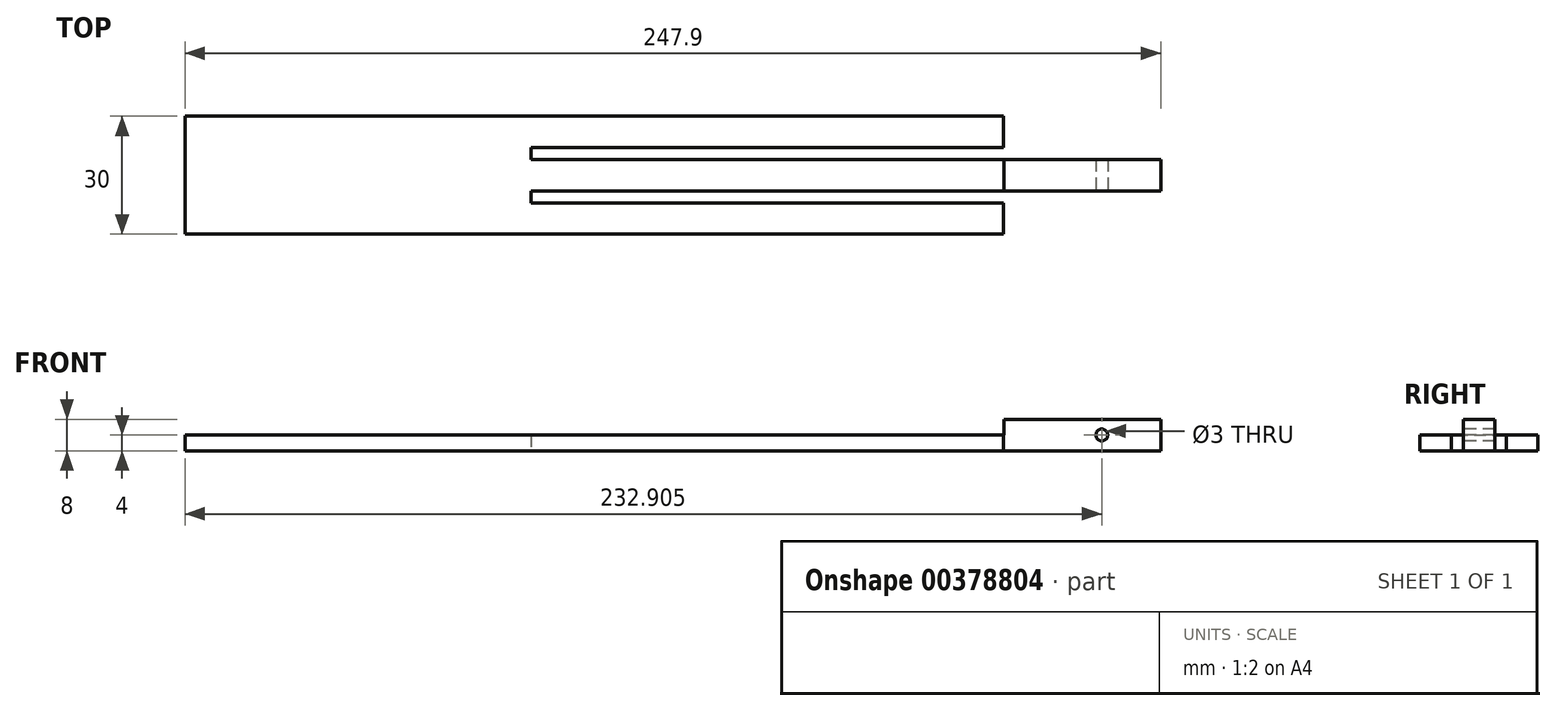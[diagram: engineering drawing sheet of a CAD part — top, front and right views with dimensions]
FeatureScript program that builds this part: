
annotation { "Feature Type Name" : "Feature", "Feature Type Description" : "" }
export const myFeature = defineFeature(function(context is Context, id is Id, definition is map)
    precondition{}
    {
        {
            var Q0;
            Q0=qCreatedBy(makeId("Top.planeOp"),FACE);
            var sketch = newSketch(context, id + "F0", { "sketchPlane" : qUnion([Q0])});
            skLineSegment(sketch, "E0.bottom", {"start": v(83.95, -15) * mm, "end": v(-123.95, -15) * mm});
            skLineSegment(sketch, "E0.top", {"start": v(83.95, 15) * mm, "end": v(-123.95, 15) * mm});
            skLineSegment(sketch, "E0.right", {"start": v(-123.95, -15) * mm, "end": v(-123.95, 15) * mm});
            skPoint(sketch, "E0.middle", {"position": v(0, 0) * mm});
            skLineSegment(sketch, "E1.bottom", {"start": v(83.95, 7) * mm, "end": v(-36.05, 7) * mm});
            skLineSegment(sketch, "E1.top", {"start": v(123.95, 4) * mm, "end": v(-36.05, 4) * mm});
            skLineSegment(sketch, "E1.right", {"start": v(-36.05, 7) * mm, "end": v(-36.05, 4) * mm});
            skLineSegment(sketch, "E2.bottom", {"start": v(123.95, -4) * mm, "end": v(-36.05, -4) * mm});
            skLineSegment(sketch, "E2.top", {"start": v(83.95, -7) * mm, "end": v(-36.05, -7) * mm});
            skLineSegment(sketch, "E2.right", {"start": v(-36.05, -4) * mm, "end": v(-36.05, -7) * mm});
            skLineSegment(sketch, "E3.trimOffspring", {"start": v(123.95, -4) * mm, "end": v(123.95, 4) * mm});
            skLineSegment(sketch, "E4.right", {"start": v(83.95, 15) * mm, "end": v(83.95, 7) * mm});
            skPoint(sketch, "E5.trimOffspring.end.orphan", {"position": v(123.95, 15) * mm});
            skLineSegment(sketch, "E6.right", {"start": v(83.95, -7) * mm, "end": v(83.95, -15) * mm});
            skPoint(sketch, "E7.orphan", {"position": v(123.95, -15) * mm});
            skSolve(sketch);
        }
        {
            var Q0;
            Q0=qSketchRegion(id+"F0",true);
            extrude(context, id + "F1", {"entities" : qUnion([Q0]), "depth" : 4 * mm});
        }
        {
            var Q0;
            Q0=makeQuery(id+"F1.opExtrude","CAP_FACE",FACE,{"disambiguationData":[OSD([sQuery(id+"F0.wireOp",EDGE,"E0.bottom"),sQuery(id+"F0.wireOp",EDGE,"E0.top"),sQuery(id+"F0.wireOp",EDGE,"E0.right"),sQuery(id+"F0.wireOp",EDGE,"E1.bottom"),sQuery(id+"F0.wireOp",EDGE,"E1.top"),sQuery(id+"F0.wireOp",EDGE,"E1.right"),sQuery(id+"F0.wireOp",EDGE,"E2.bottom"),sQuery(id+"F0.wireOp",EDGE,"E2.top"),sQuery(id+"F0.wireOp",EDGE,"E2.right"),sQuery(id+"F0.wireOp",EDGE,"E3.trimOffspring"),sQuery(id+"F0.wireOp",EDGE,"E4.right"),sQuery(id+"F0.wireOp",EDGE,"E6.right")])],"isStart":false});
            var sketch = newSketch(context, id + "F2", { "sketchPlane" : qUnion([Q0])});
            skLineSegment(sketch, "E8.bottom", {"start": v(123.95, 4) * mm, "end": v(84.13, 4) * mm});
            skLineSegment(sketch, "E8.top", {"start": v(123.95, -4) * mm, "end": v(84.13, -4) * mm});
            skLineSegment(sketch, "E8.left", {"start": v(123.95, 4) * mm, "end": v(123.95, -4) * mm});
            skLineSegment(sketch, "E8.right", {"start": v(84.13, 4) * mm, "end": v(84.13, -4) * mm});
            skSolve(sketch);
        }
        {
            var Q0;
            Q0=qSketchRegion(id+"F2",true);
            extrude(context, id + "F3", {"entities" : qUnion([Q0]), "operationType" : NewBodyOperationType.ADD, "depth" : 4 * mm});
        }
        {
            var Q0;
            Q0=makeQuery(id+"F3.boolean.opBoolean","MERGE",FACE,{"derivedFrom":[makeQuery(id+"F1.opExtrude","SWEPT_FACE",FACE,{"disambiguationData":[OSD([sQuery(id+"F0.wireOp",EDGE,"E2.bottom")])]}),makeQuery(id+"F3.opExtrude","SWEPT_FACE",FACE,{"disambiguationData":[OSD([sQuery(id+"F2.wireOp",EDGE,"E8.top")])]})]});
            var sketch = newSketch(context, id + "F4", { "sketchPlane" : qUnion([Q0])});
            skCircle(sketch, "E9", {"center": v(108.95, 4) * mm, "radius": 1.5 * mm});
            skPoint(sketch, "E10.bottom.end.orphan", {"position": v(108.95, 8) * mm});
            skPoint(sketch, "E10.top.end.orphan", {"position": v(108.95, 0) * mm});
            skSolve(sketch);
        }
        {
            var Q0;
            Q0=makeQuery(id+"F4.imprint","IMPRINT",FACE,{"disambiguationData":[TD([[makeQuery(id+"F4.imprint","IMPRINT",EDGE,{"derivedFrom":sQuery(id+"F4.wireOp",EDGE,"E9")}),1.0]])]});
            extrude(context, id + "F5", {"entities" : qUnion([Q0]), "operationType" : NewBodyOperationType.REMOVE, "oppositeDirection" : true, "depth" : 12 * mm});
        }
    });
